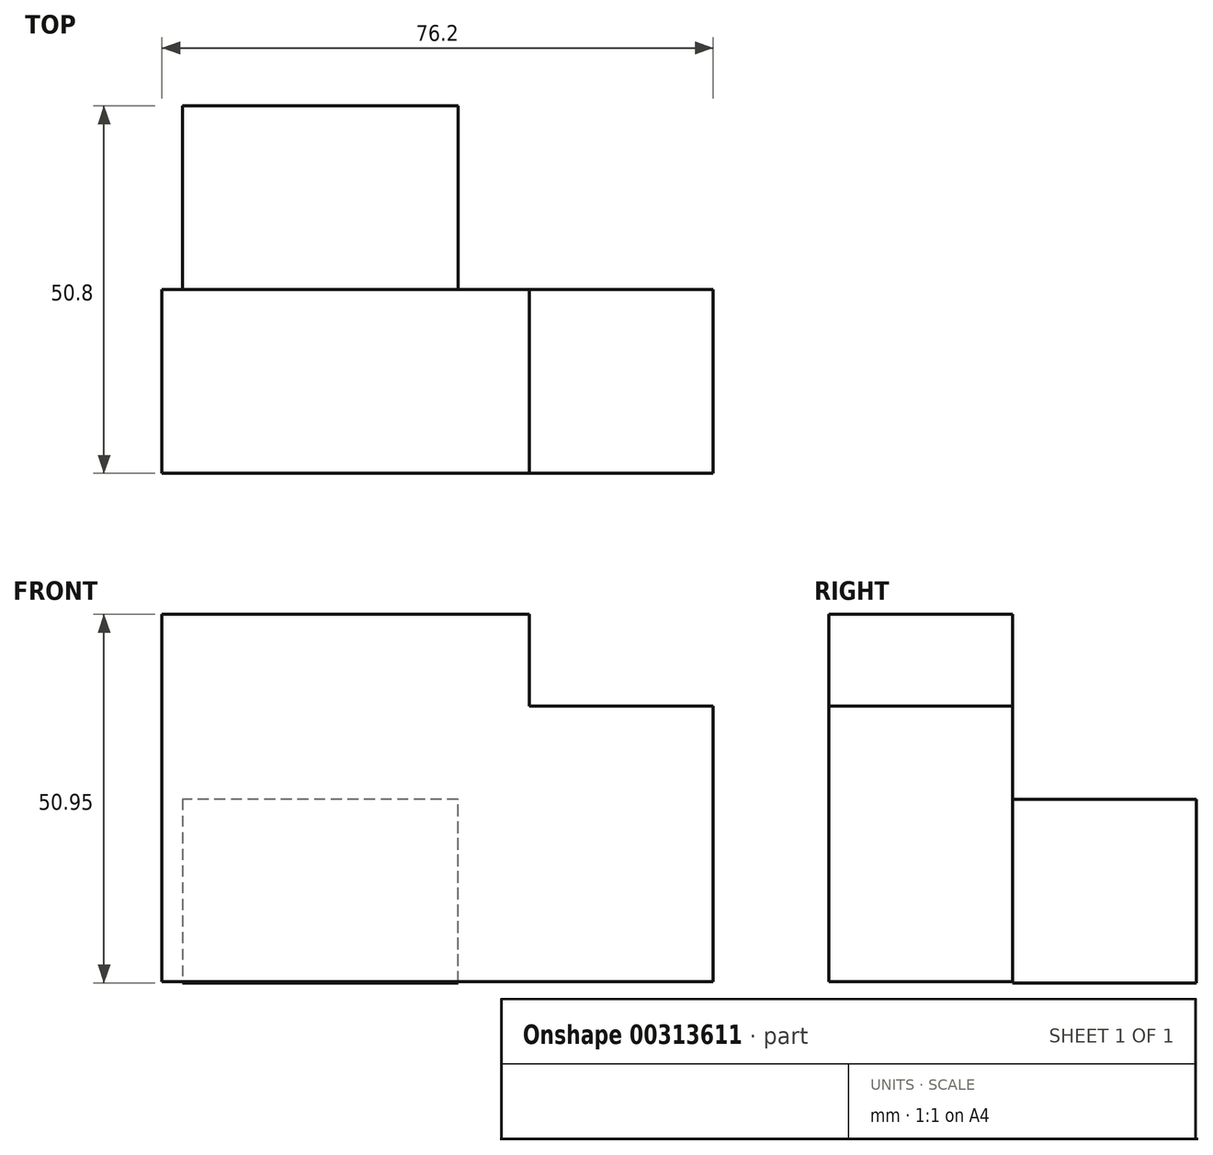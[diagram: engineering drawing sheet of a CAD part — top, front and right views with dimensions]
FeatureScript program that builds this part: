
annotation { "Feature Type Name" : "Feature", "Feature Type Description" : "" }
export const myFeature = defineFeature(function(context is Context, id is Id, definition is map)
    precondition{}
    {
        {
            var Q0;
            Q0=qCreatedBy(makeId("Front.planeOp"),FACE);
            var sketch = newSketch(context, id + "F0", { "sketchPlane" : qUnion([Q0])});
            skLineSegment(sketch, "E0", {"start": v(-38.8, -55.33) * mm, "end": v(37.4, -55.33) * mm});
            skLineSegment(sketch, "E1", {"start": v(37.4, -55.33) * mm, "end": v(37.4, -17.23) * mm});
            skLineSegment(sketch, "E2", {"start": v(37.4, -17.23) * mm, "end": v(12, -17.23) * mm});
            skLineSegment(sketch, "E3", {"start": v(12, -17.23) * mm, "end": v(12, -4.53) * mm});
            skLineSegment(sketch, "E4", {"start": v(12, -4.53) * mm, "end": v(-38.8, -4.53) * mm});
            skLineSegment(sketch, "E5", {"start": v(-38.8, -4.53) * mm, "end": v(-38.8, -58.45) * mm});
            skSolve(sketch);
        }
        {
            var Q0;
            {var subQ0=sQuery(id+"F0.wireOp",EDGE,"E0");Q0=makeQuery(id+"F0.imprint","IMPRINT",FACE,{"disambiguationData":[TD([[makeQuery(id+"F0.imprint","IMPRINT",EDGE,{"derivedFrom":subQ0}),1.0]])]});}
            extrude(context, id + "F1", {"entities" : qUnion([Q0]), "depth" : 25.4 * mm});
        }
        {
            var Q0;
            Q0=qCreatedBy(makeId("Front.planeOp"),FACE);
            var sketch = newSketch(context, id + "F2", { "sketchPlane" : qUnion([Q0])});
            skLineSegment(sketch, "E6", {"start": v(-35.96, -55.48) * mm, "end": v(2.14, -55.48) * mm});
            skLineSegment(sketch, "E7", {"start": v(2.14, -55.48) * mm, "end": v(2.14, -30.08) * mm});
            skLineSegment(sketch, "E8", {"start": v(2.14, -30.08) * mm, "end": v(-35.96, -30.08) * mm});
            skLineSegment(sketch, "E9", {"start": v(-35.96, -30.08) * mm, "end": v(-35.96, -55.48) * mm});
            skSolve(sketch);
        }
        {
            var Q0;
            Q0 = qSketchRegion(id + "F2", true);
            var Q1;
            Q1=makeQuery(id+"F1.opExtrude","CAP_FACE",FACE,{"disambiguationData":[OSD([sQuery(id+"F0.wireOp",EDGE,"E0"),sQuery(id+"F0.wireOp",EDGE,"E1"),sQuery(id+"F0.wireOp",EDGE,"E2"),sQuery(id+"F0.wireOp",EDGE,"E3"),sQuery(id+"F0.wireOp",EDGE,"E4"),sQuery(id+"F0.wireOp",EDGE,"E5")])],"isStart":false});
            extrude(context, id + "F3", {"entities" : qUnion([Q0, Q1]), "operationType" : NewBodyOperationType.ADD, "oppositeDirection" : true, "depth" : 25.4 * mm});
        }
    });
